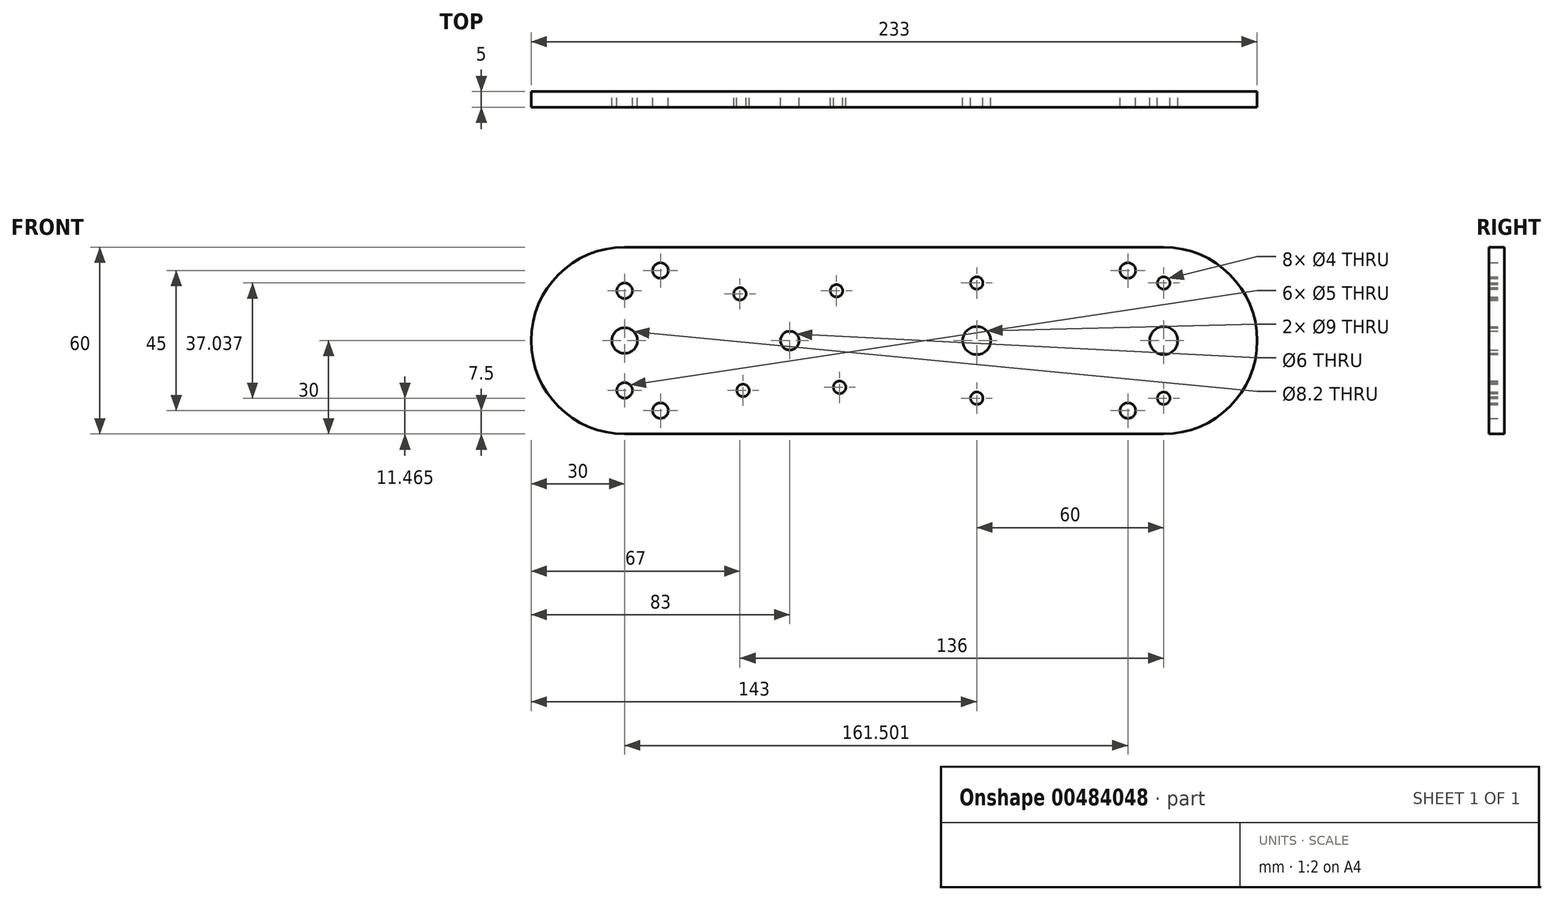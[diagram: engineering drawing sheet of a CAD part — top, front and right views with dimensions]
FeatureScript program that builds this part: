
annotation { "Feature Type Name" : "Feature", "Feature Type Description" : "" }
export const myFeature = defineFeature(function(context is Context, id is Id, definition is map)
    precondition{}
    {
        {
            var Q0;
            Q0=qCreatedBy(makeId("Front.planeOp"),FACE);
            var sketch = newSketch(context, id + "F0", { "sketchPlane" : qUnion([Q0])});
            skLineSegment(sketch, "E0.bottom", {"start": v(0, 0) * mm, "end": v(-173, 0) * mm});
            skLineSegment(sketch, "E0.top", {"start": v(0, 60) * mm, "end": v(-173, 60) * mm});
            skArc(sketch, "E1", {"start": v(0, 0) * mm, "mid": v(30, 30) * mm, "end": v(0, 60) * mm});
            skPoint(sketch, "E2.middle", {"position": v(-120, 30) * mm});
            skCircle(sketch, "E3", {"center": v(-104, 15) * mm, "radius": 2 * mm});
            skCircle(sketch, "E4", {"center": v(-135, 14) * mm, "radius": 2 * mm});
            skCircle(sketch, "E5", {"center": v(-105, 46) * mm, "radius": 2 * mm});
            skCircle(sketch, "E6", {"center": v(-136, 45) * mm, "radius": 2 * mm});
            skCircle(sketch, "E7", {"center": v(-120, 30) * mm, "radius": 3 * mm});
            skCircle(sketch, "E8", {"center": v(-60, 48.5) * mm, "radius": 2 * mm});
            skCircle(sketch, "E9", {"center": v(-60, 11.5) * mm, "radius": 2 * mm});
            skCircle(sketch, "E10", {"center": v(-60, 30) * mm, "radius": 4.5 * mm});
            skArc(sketch, "E11", {"start": v(-173, 0) * mm, "mid": v(-203, 30) * mm, "end": v(-173, 60) * mm});
            skCircle(sketch, "E12", {"center": v(0, 48.5) * mm, "radius": 2 * mm});
            skCircle(sketch, "E13", {"center": v(0, 11.46) * mm, "radius": 2 * mm});
            skCircle(sketch, "E14", {"center": v(0, 30) * mm, "radius": 4.5 * mm});
            skCircle(sketch, "E15", {"center": v(-173, 46) * mm, "radius": 2.5 * mm});
            skCircle(sketch, "E16", {"center": v(-173, 14) * mm, "radius": 2.5 * mm});
            skPoint(sketch, "E17.middle", {"position": v(-86.5, 30) * mm});
            skCircle(sketch, "E18", {"center": v(-11.5, 7.5) * mm, "radius": 2.5 * mm});
            skCircle(sketch, "E19", {"center": v(-11.5, 52.5) * mm, "radius": 2.5 * mm});
            skCircle(sketch, "E20", {"center": v(-161.5, 52.5) * mm, "radius": 2.5 * mm});
            skCircle(sketch, "E21", {"center": v(-161.5, 7.5) * mm, "radius": 2.5 * mm});
            skCircle(sketch, "E22", {"center": v(-173, 30) * mm, "radius": 4.1 * mm});
            skSolve(sketch);
        }
        {
            var Q0;
            Q0=makeQuery(id+"F0.imprint","IMPRINT",FACE,{"disambiguationData":[TD([[makeQuery(id+"F0.imprint","IMPRINT",EDGE,{"derivedFrom":sQuery(id+"F0.wireOp",EDGE,"E0.bottom")}),-1.0]])]});
            extrude(context, id + "F1", {"entities" : qUnion([Q0]), "depth" : 5 * mm});
        }
    });
